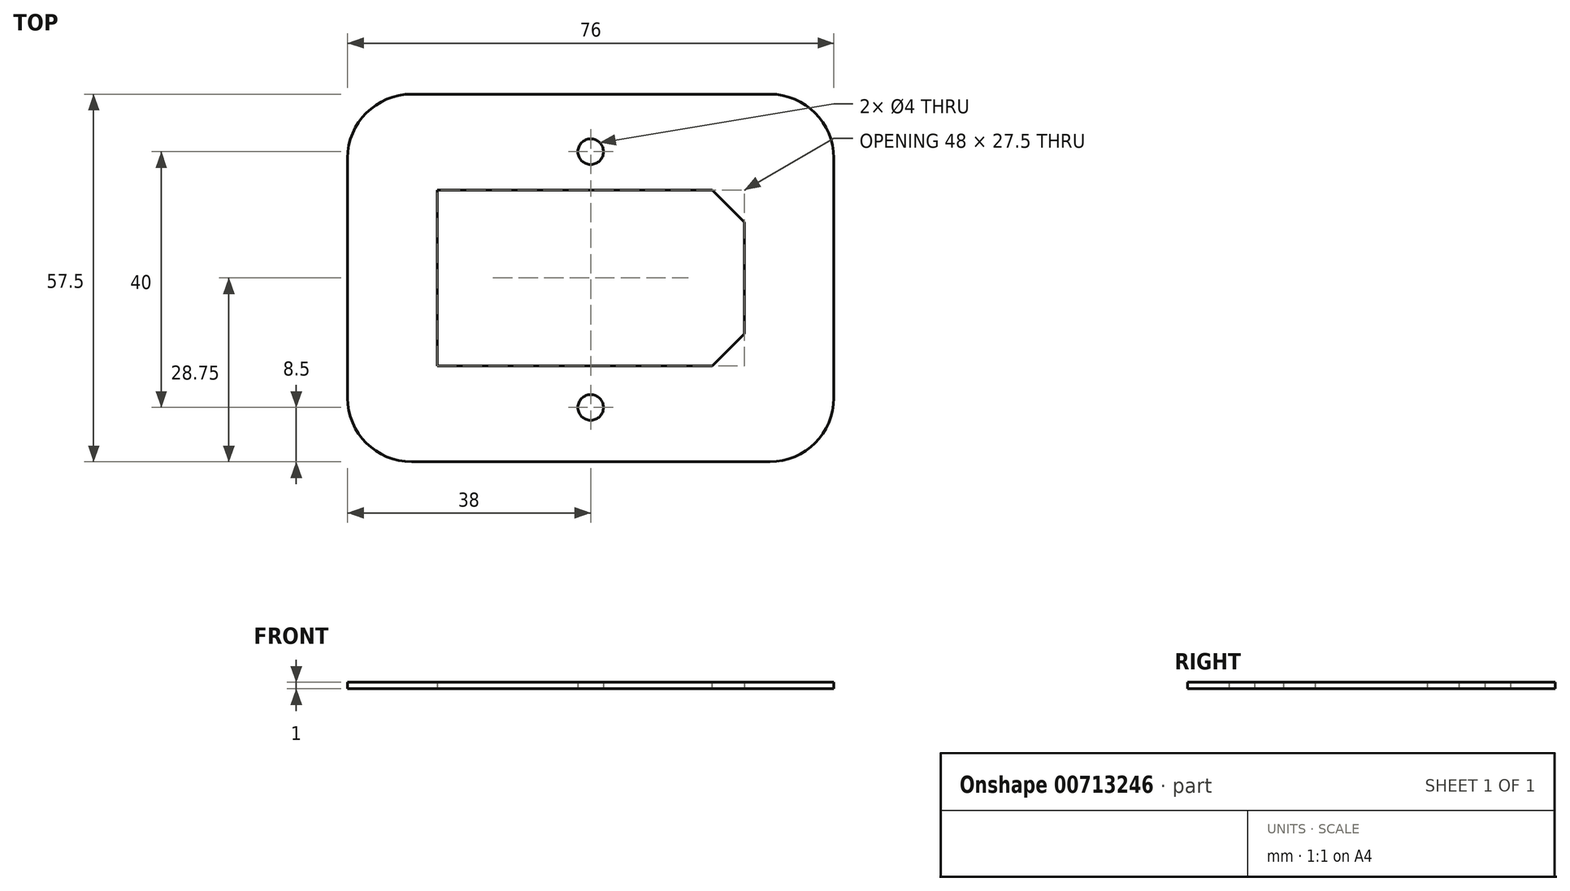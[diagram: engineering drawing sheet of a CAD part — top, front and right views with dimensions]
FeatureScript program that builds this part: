
annotation { "Feature Type Name" : "Feature", "Feature Type Description" : "" }
export const myFeature = defineFeature(function(context is Context, id is Id, definition is map)
    precondition{}
    {
        {
            var Q0;
            Q0=qCreatedBy(makeId("Top.planeOp"),FACE);
            var sketch = newSketch(context, id + "F0", { "sketchPlane" : qUnion([Q0])});
            skLineSegment(sketch, "E0.bottom", {"start": v(24, 13.75) * mm, "end": v(-24, 13.75) * mm});
            skLineSegment(sketch, "E0.top", {"start": v(24, -13.75) * mm, "end": v(-24, -13.75) * mm});
            skLineSegment(sketch, "E0.left", {"start": v(24, 13.75) * mm, "end": v(24, -13.75) * mm});
            skLineSegment(sketch, "E0.right", {"start": v(-24, 13.75) * mm, "end": v(-24, -13.75) * mm});
            skPoint(sketch, "E0.middle", {"position": v(0, 0) * mm});
            skCircle(sketch, "E1", {"center": v(0, 19.75) * mm, "radius": 2 * mm});
            skCircle(sketch, "E2", {"center": v(0, -20.25) * mm, "radius": 2 * mm});
            skLineSegment(sketch, "E3.bottom", {"start": v(-38, 28.75) * mm, "end": v(38, 28.75) * mm});
            skLineSegment(sketch, "E3.top", {"start": v(-38, -28.75) * mm, "end": v(38, -28.75) * mm});
            skLineSegment(sketch, "E3.left", {"start": v(-38, 28.75) * mm, "end": v(-38, -28.75) * mm});
            skLineSegment(sketch, "E3.right", {"start": v(38, 28.75) * mm, "end": v(38, -28.75) * mm});
            skSolve(sketch);
        }
        {
            var Q0;
            Q0=makeQuery(id+"F0.imprint","IMPRINT",FACE,{"disambiguationData":[TD([[makeQuery(id+"F0.imprint","IMPRINT",EDGE,{"derivedFrom":sQuery(id+"F0.wireOp",EDGE,"E0.bottom")}),-1.0]])]});
            extrude(context, id + "F1", {"entities" : qUnion([Q0]), "depth" : (1) * mm, "offsetDistance" : 25 * mm});
        }
        {
            var Q0;
            Q0=makeQuery(id+"F1.opExtrude","SWEPT_EDGE",EDGE,{"disambiguationData":[OSD([sQuery(id+"F0.wireOp",EDGE,"E3.bottom"),sQuery(id+"F0.wireOp",EDGE,"E3.left")])]});
            var Q1;
            Q1=makeQuery(id+"F1.opExtrude","SWEPT_EDGE",EDGE,{"disambiguationData":[OSD([sQuery(id+"F0.wireOp",EDGE,"E3.top"),sQuery(id+"F0.wireOp",EDGE,"E3.left")])]});
            var Q2;
            Q2=makeQuery(id+"F1.opExtrude","SWEPT_EDGE",EDGE,{"disambiguationData":[OSD([sQuery(id+"F0.wireOp",EDGE,"E3.bottom"),sQuery(id+"F0.wireOp",EDGE,"E3.right")])]});
            var Q3;
            Q3=makeQuery(id+"F1.opExtrude","SWEPT_EDGE",EDGE,{"disambiguationData":[OSD([sQuery(id+"F0.wireOp",EDGE,"E3.top"),sQuery(id+"F0.wireOp",EDGE,"E3.right")])]});
            fillet(context, id + "F2", {"entities" : qUnion([Q0, Q1, Q2, Q3]), "radius" : 10 * mm, "tangentPropagation" : true, "allowEdgeOverflow" : false});
        }
        {
            var Q0;
            Q0=makeQuery(id+"F1.opExtrude","SWEPT_EDGE",EDGE,{"disambiguationData":[OSD([sQuery(id+"F0.wireOp",EDGE,"E0.bottom"),sQuery(id+"F0.wireOp",EDGE,"E0.left")])]});
            var Q1;
            Q1=makeQuery(id+"F1.opExtrude","SWEPT_EDGE",EDGE,{"disambiguationData":[OSD([sQuery(id+"F0.wireOp",EDGE,"E0.top"),sQuery(id+"F0.wireOp",EDGE,"E0.left")])]});
            chamfer(context, id + "F3", {"entities" : qUnion([Q0, Q1]), "width" : 5 * mm, "tangentPropagation" : true});
        }
    });
